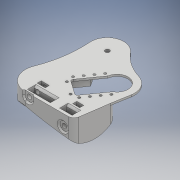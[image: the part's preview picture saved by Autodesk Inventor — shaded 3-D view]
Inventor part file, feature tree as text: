
AUTODESK INVENTOR PART (.ipt)
format: ipt  version: 2017 (Build 210142000, 142)  size: 711,680 bytes
history: native  units: mm
features: sketch x13, other x4, plane x3, extrude x1, hole x1
ambient origin geometry x8: Origin, YZ Plane, XZ Plane, XY Plane, X Axis, Y Axis, Z Axis, Center Point
bodies: Solid1 (feature_tree)
feature tree (22):
  other  "Arm - shoulder R.ipt"
  plane  "Work Plane3"
  extrude  "Extrusion1"  Depth=10.0mm TaperAngle=0.0deg
  hole  "Hole1"  [1 undecoded]
  other  "Solid1::Arm - shoulder R.ipt"
  other  "Solid2::Arm - shoulder R.ipt"
  other  "TaggingFeature1"
  sketch  "Sketch1"  dims[d0=10.0mm d1=22.077367mm d2=0.0mm]
  sketch  "Sketch2"  dims[d3=10.0mm d4=10.0mm]
  sketch  "Sketch3"  dims[d5=4.5mm d6=6.0mm d7=4.0mm d8=2.0mm d9=90.0deg d10=8.0mm d11=20.594885mm d14=1.745329mm]
  sketch  "Sketch4"
  sketch  "Sketch5"
  sketch  "Sketch6"
  sketch  "Sketch7"
  sketch  "Sketch8"
  sketch  "Sketch9"
  sketch  "Sketch10"
  sketch  "Sketch12"
  sketch  "Sketch13"
  plane  "Work Plane1"
  plane  "Work Plane2"
  sketch  "Sketch14"
note: 1 required parameter value undecoded (feature->parameter linkage not recoverable at this tier; creation-order binding heuristic only, values carry confidence <= 0.55)
